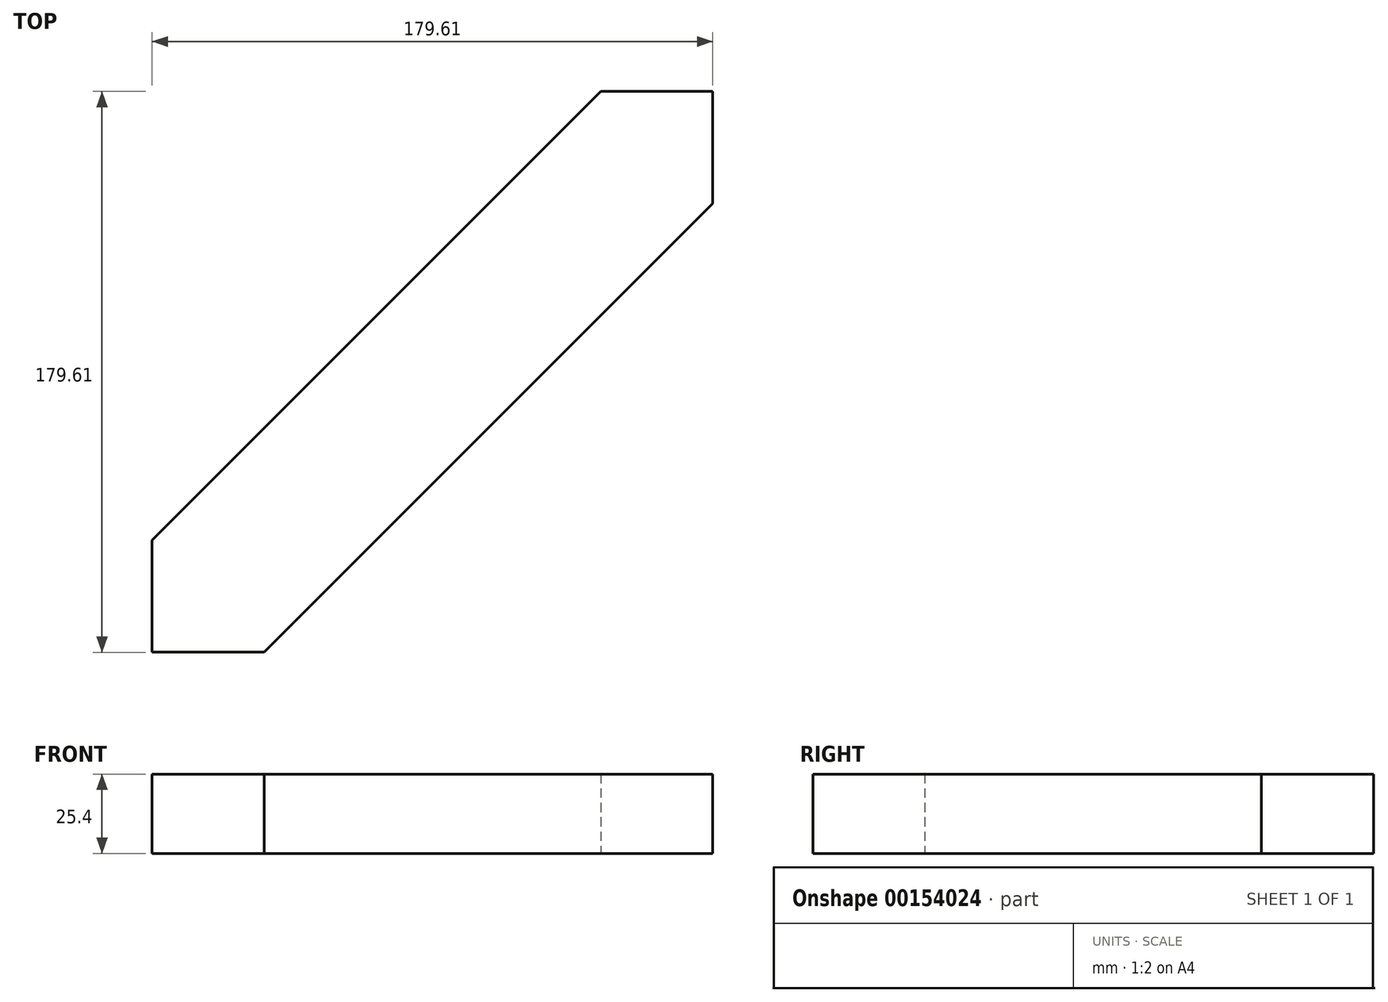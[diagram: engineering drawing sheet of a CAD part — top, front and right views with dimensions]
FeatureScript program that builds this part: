
annotation { "Feature Type Name" : "Feature", "Feature Type Description" : "" }
export const myFeature = defineFeature(function(context is Context, id is Id, definition is map)
    precondition{}
    {
        {
            var Q0;
            Q0=qCreatedBy(makeId("Top.planeOp"),FACE);
            var sketch = newSketch(context, id + "F0", { "sketchPlane" : qUnion([Q0])});
            skLineSegment(sketch, "E0", {"start": v(0, 0) * mm, "end": v(0, -179.6) * mm, "construction": true});
            skLineSegment(sketch, "E1", {"start": v(35.92, -179.6) * mm, "end": v(179.6, -35.92) * mm});
            skLineSegment(sketch, "E2", {"start": v(179.6, 0) * mm, "end": v(0, 0) * mm, "construction": true});
            skLineSegment(sketch, "E3", {"start": v(0, -179.6) * mm, "end": v(0, -143.68) * mm});
            skLineSegment(sketch, "E4", {"start": v(0, -143.68) * mm, "end": v(143.68, 0) * mm});
            skLineSegment(sketch, "E5", {"start": v(143.68, 0) * mm, "end": v(179.6, 0) * mm});
            skLineSegment(sketch, "E6", {"start": v(0, -179.6) * mm, "end": v(35.92, -179.6) * mm});
            skLineSegment(sketch, "E7", {"start": v(179.6, 0) * mm, "end": v(179.6, -35.92) * mm});
            skPoint(sketch, "E8.orphan", {"position": v(0, -215.53) * mm});
            skPoint(sketch, "E9.orphan", {"position": v(215.53, 0) * mm});
            skSolve(sketch);
        }
        {
            var Q0;
            Q0 = qSketchRegion(id + "F0", true);
            extrude(context, id + "F1", {"entities" : qUnion([Q0]), "depth" : 25.4 * mm});
        }
    });
